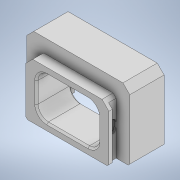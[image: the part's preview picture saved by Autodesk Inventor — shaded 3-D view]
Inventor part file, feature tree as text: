
AUTODESK INVENTOR PART (.ipt)
format: ipt  version: 2020.2 (Build 242310000, 310)  size: 296,448 bytes
history: native  units: mm
features: extrude x7, sketch x7, projected_geometry x3, fillet x2, chamfer x2, mirror x1
ambient origin geometry x8: Origin, YZ Plane, XZ Plane, XY Plane, X Axis, Y Axis, Z Axis, Center Point
bodies: Solid1 (feature_tree)
feature tree (22):
  extrude  "Extrusion1"  Depth=20.0mm
  extrude  "Extrusion2"  Depth=12.0mm
  extrude  "Extrusion3"  Depth=22.0mm
  extrude  "Extrusion4"  Depth=2.2mm TaperAngle=0.0deg
  extrude  "Extrusion5"  Depth=1.0mm TaperAngle=0.0deg
  extrude  "Extrusion6"  Depth=0.6mm TaperAngle=0.0deg
  fillet  "Fillet3"  Radius=6.8mm
  fillet  "Fillet1"  Radius=1.5mm
  mirror  "Mirror1"
  chamfer  "Chamfer1"  Distance=16.0mm
  chamfer  "Chamfer2"  Distance=3.0mm
  extrude  "Extrusion7"  Depth=22.3mm
  sketch  "Sketch1"  dims[d0=30.0mm d1=20.0mm]
  sketch  "Sketch2"  dims[d2=18.0mm d3=12.0mm]
  projected_geometry  "Projected Loop1"
  sketch  "Sketch3"  dims[d4=7.0mm d5=0.0mm d6=22.0mm]
  sketch  "Sketch4"  dims[d7=16.0mm d8=2.2mm d9=0.0mm]
  projected_geometry  "Projected Loop2"
  sketch  "Sketch5"  dims[d10=24.2mm d11=1.0mm d12=0.0mm]
  projected_geometry  "Projected Loop3"
  sketch  "Sketch6"  dims[d13=2.0mm d17=0.6mm d18=0.0mm d19=6.8mm d20=1.5mm]
  sketch  "Sketch8"  dims[d21=25.0mm d22=16.0mm d23=3.0mm d24=0.0mm d26=22.3mm d27=11.15mm d28=21.6mm d29=10.8mm d30=45.0deg d31=45.0deg d32=45.0deg d33=45.0deg d34=7.5mm d35=2.0mm d36=1.4mm d37=0.0mm d38=3.0mm d40=2.0mm d41=2.0mm d42=2.0mm d43=45.0deg d44=0.5mm d45=2.0mm d46=45.0deg d47=10.0mm d48=0.0mm]
